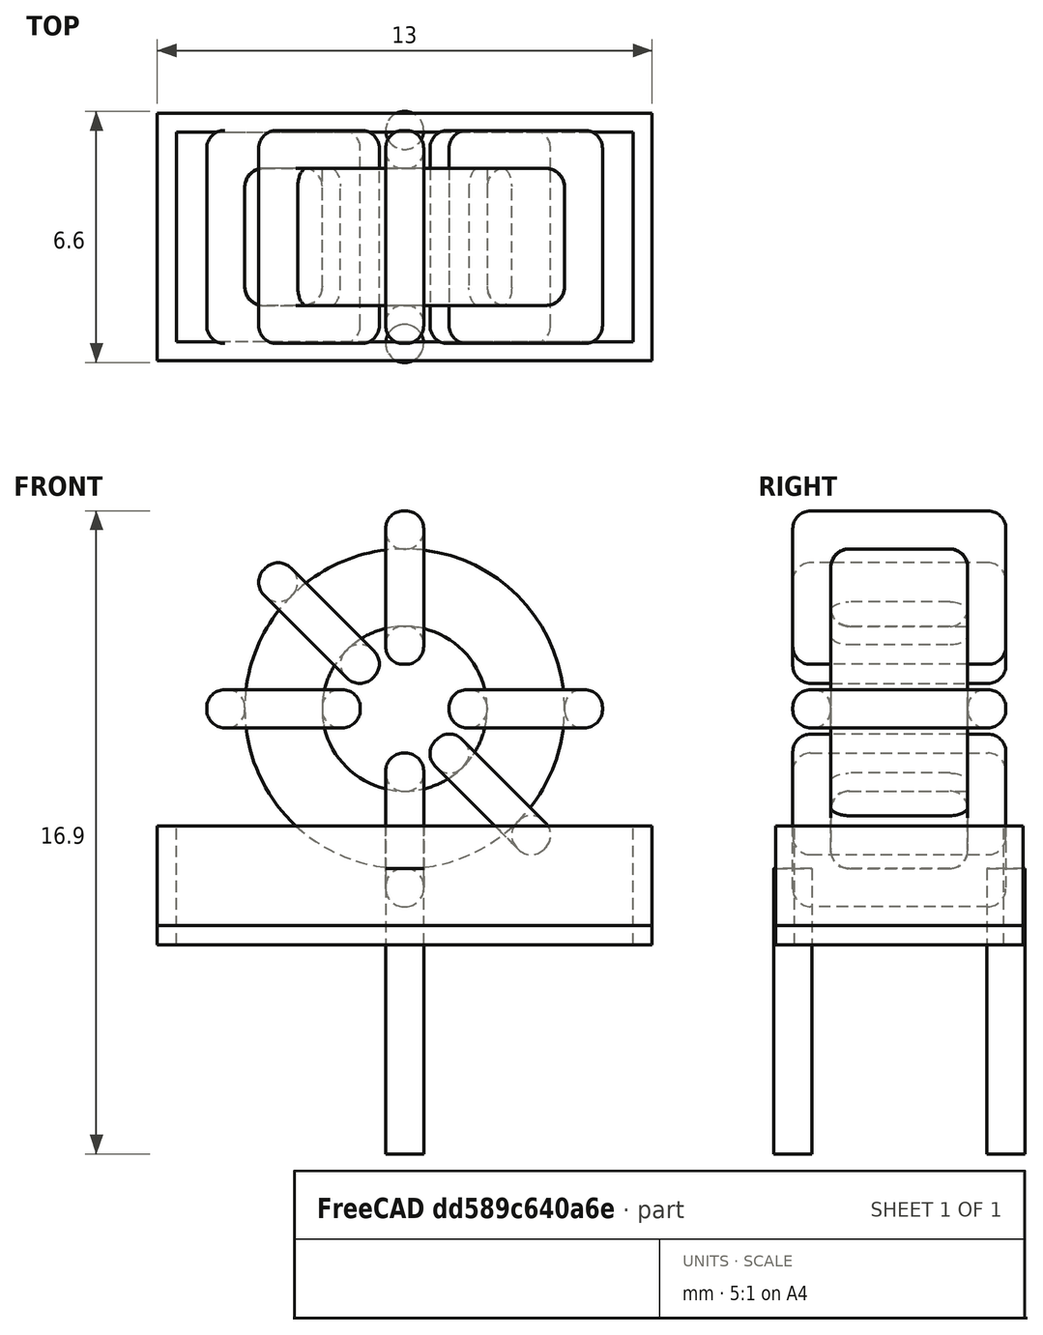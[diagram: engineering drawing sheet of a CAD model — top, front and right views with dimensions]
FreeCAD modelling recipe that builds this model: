
FCSTD DOCUMENT  (FreeCAD 0.16R6703 (Git))
Label: L_Toroid_Vertical_L13.0mm_W6.5mm_P5.60mm
License: All rights reserved
LicenseURL: http://en.wikipedia.org/wiki/All_rights_reserved
objects: Sketcher::SketchObject×8, PartDesign::Pad×8, PartDesign::Fillet×5, Spreadsheet::Sheet×1
note: 29 computed .brp shape members not serialized (recipe doc carries the construction recipe); baked Part::Feature solids carry a one-line shape summary decoded from their .brp

FEATURE [Spreadsheet::Sheet] Spreadsheet  label="dimensions"
  cells = A1=Wx; B1(Wx)=10.4; C1(WW)=4.333333333333333; D1(iWx)=13; A2=Wy; B2(Wy)=5.6; D2(iWy)=6.5; A3=RM; B3(RMx)=5.6; C3(RMy)=0; A4=d_wire; B4(d_wire)=1; A5=H; B5(H)=13; A6=offsetx; B6(offsetx)=6.5
FEATURE [Sketcher::SketchObject] Sketch
  Placement = pos=(0,-2.8,0) rot=(1,0,0;1.5708rad)
  expr: Placement.Base.y = -Spreadsheet.RMx / 2
  expr: Constraints[0] = Spreadsheet.Wx / 2 - Spreadsheet.d_wire
  expr: Constraints[4] = Spreadsheet.WW / 2
  expr: Constraints[2] = Spreadsheet.Wx / 2 + Spreadsheet.d_wire + 0.5
  sketch-geometry (2):
    g0: Circle CenterX=0 CenterY=6.7 CenterZ=0 NormalX=0 NormalY=0 NormalZ=1 Radius=4.2
    g1: Circle CenterX=0 CenterY=6.7 CenterZ=0 NormalX=0 NormalY=0 NormalZ=1 Radius=2.16667
  constraints (5):
    c: Radius(g0) = 4.2
    c: DistanceX(g-1,g0) = 0
    c: DistanceY(g-1,g0) = 6.7
    c: Coincident(g1,g0)
    c: Radius(g1) = 2.16667
FEATURE [PartDesign::Pad] Pad
  Length = 3.6
  Length2 = 100
  Midplane = true
  Placement = pos=(0,-2.8,0) rot=(1,0,0;1.5708rad)
  Sketch = -> Sketch
  Type = 0
  expr: Length = Spreadsheet.Wy - 2 * Spreadsheet.d_wire
FEATURE [Sketcher::SketchObject] Sketch001
  Placement = pos=(0,0,1.5) rot=(0,0,1;0rad)
  expr: Placement.Base.z = 0.5 + Spreadsheet.d_wire
  expr: Constraints[4] = Spreadsheet.RMy
  expr: Constraints[2] = -Spreadsheet.RMx
  expr: Constraints[1] = Spreadsheet.d_wire / 2
  sketch-geometry (2):
    g0: Circle CenterX=0 CenterY=0 CenterZ=0 NormalX=0 NormalY=0 NormalZ=1 Radius=0.5
    g1: Circle CenterX=0 CenterY=-5.6 CenterZ=0 NormalX=0 NormalY=0 NormalZ=1 Radius=0.5
  constraints (5):
    c: Equal(g0,g1)
    c: Radius(g0) = 0.5
    c: DistanceY(g-1,g1) = -5.6
    c: Coincident(g0,g-1)
    c: DistanceX(g-1,g1) = 0
FEATURE [PartDesign::Pad] Pad001
  Length = 1
  Length2 = 6.5
  Placement = pos=(0,0,1.5) rot=(0,0,1;0rad)
  Reversed = true
  Sketch = -> Sketch001
  Type = 4
  expr: Length2 = 5.5 + Spreadsheet.d_wire
  expr: Length = Spreadsheet.d_wire
FEATURE [PartDesign::Fillet] Fillet
  Base = -> Pad [Edge6,Edge3,Edge2]
  Placement = pos=(0,-2.8,0) rot=(1,0,0;1.5708rad)
  Radius = 0.5
FEATURE [Sketcher::SketchObject] Sketch003
  Placement = pos=(0,0,6.7) rot=(1,0,0;3.14159rad)
  expr: Constraints[18] = Spreadsheet.d_wire
  expr: Constraints[16] = Spreadsheet.d_wire
  expr: Constraints[19] = Spreadsheet.d_wire
  expr: Constraints[17] = Spreadsheet.d_wire
  expr: Placement.Base.y = -1 * (Spreadsheet.RMx - Spreadsheet.Wy) / 2
  expr: Constraints[21] = (Spreadsheet.Wx - Spreadsheet.WW) / 2 - Spreadsheet.d_wire
  expr: Constraints[22] = Spreadsheet.Wx / 2 - Spreadsheet.d_wire
  expr: Constraints[43] = Spreadsheet.d_wire
  expr: Constraints[48] = Spreadsheet.Wx - Spreadsheet.d_wire * 2
  expr: Constraints[49] = Spreadsheet.Wy
  expr: Placement.Base.z = Spreadsheet.Wx / 2 + Spreadsheet.d_wire + 0.5
  sketch-geometry (16):
    g0: LineSegment StartX=-1.16667 StartY=0 StartZ=0 EndX=-5.2 EndY=0 EndZ=0
    g1: LineSegment StartX=-5.2 StartY=0 StartZ=0 EndX=-5.2 EndY=5.6 EndZ=0
    g2: LineSegment StartX=-5.2 StartY=5.6 StartZ=0 EndX=-1.16667 EndY=5.6 EndZ=0
    g3: LineSegment StartX=-1.16667 StartY=5.6 StartZ=0 EndX=-1.16667 EndY=0 EndZ=0
    g4: LineSegment StartX=-4.2 StartY=4.6 StartZ=0 EndX=-2.16667 EndY=4.6 EndZ=0
    g5: LineSegment StartX=-2.16667 StartY=4.6 StartZ=0 EndX=-2.16667 EndY=1 EndZ=0
    g6: LineSegment StartX=-2.16667 StartY=1 StartZ=0 EndX=-4.2 EndY=1 EndZ=0
    g7: LineSegment StartX=-4.2 StartY=1 StartZ=0 EndX=-4.2 EndY=4.6 EndZ=0
    g8: LineSegment StartX=1.16667 StartY=5.6 StartZ=0 EndX=5.2 EndY=5.6 EndZ=0
    g9: LineSegment StartX=5.2 StartY=5.6 StartZ=0 EndX=5.2 EndY=0 EndZ=0
    g10: LineSegment StartX=5.2 StartY=0 StartZ=0 EndX=1.16667 EndY=0 EndZ=0
    g11: LineSegment StartX=1.16667 StartY=0 StartZ=0 EndX=1.16667 EndY=5.6 EndZ=0
    g12: LineSegment StartX=2.16667 StartY=4.6 StartZ=0 EndX=4.2 EndY=4.6 EndZ=0
    g13: LineSegment StartX=4.2 StartY=4.6 StartZ=0 EndX=4.2 EndY=1 EndZ=0
    g14: LineSegment StartX=4.2 StartY=1 StartZ=0 EndX=2.16667 EndY=1 EndZ=0
    g15: LineSegment StartX=2.16667 StartY=1 StartZ=0 EndX=2.16667 EndY=4.6 EndZ=0
  constraints (50):
    c: Horizontal(g0)
    c: Coincident(g1,g0)
    c: Vertical(g1)
    c: Coincident(g2,g1)
    c: Horizontal(g2)
    c: Coincident(g3,g2)
    c: Coincident(g3,g0)
    c: Vertical(g3)
    c: Coincident(g4,g5)
    c: Coincident(g5,g6)
    c: Coincident(g6,g7)
    c: Coincident(g7,g4)
    c: Horizontal(g4)
    c: Horizontal(g6)
    c: Vertical(g5)
    c: Vertical(g7)
    c: DistanceX(g1,g4) = 1
    c: DistanceY(g4,g1) = 1
    c: DistanceX(g5,g0) = 1
    c: DistanceY(g0,g5) = 1
    c: DistanceY(g-1,g0) = 0
    c: DistanceX(g6,g6) = 2.03333
    c: DistanceX(g6,g-1) = 4.2
    c: Coincident(g8,g9)
    c: Coincident(g9,g10)
    c: Coincident(g10,g11)
    c: Coincident(g11,g8)
    c: Horizontal(g8)
    c: Horizontal(g10)
    c: Vertical(g9)
    c: Vertical(g11)
    c: Coincident(g12,g13)
    c: Coincident(g13,g14)
    c: Coincident(g14,g15)
    c: Coincident(g15,g12)
    c: Horizontal(g12)
    c: Horizontal(g14)
    c: Vertical(g13)
    c: Vertical(g15)
    c: DistanceY(g8,g2) = 0
    c: DistanceY(g10,g0) = 0
    c: DistanceY(g14,g5) = 0
    c: DistanceY(g12,g4) = 0
    c: DistanceX(g8,g12) = 1
    c: Equal(g8,g2)
    c: Equal(g12,g4)
    c: Equal(g9,g1)
    c: Equal(g13,g7)
    c: DistanceX(g4,g12) = 8.4
    c: DistanceY(g0,g1) = 5.6
FEATURE [PartDesign::Pad] Pad002
  Length = 1
  Length2 = 100
  Midplane = true
  Placement = pos=(0,0,6.7) rot=(1,0,0;3.14159rad)
  Sketch = -> Sketch003
  Type = 0
  expr: Length = Spreadsheet.d_wire
FEATURE [PartDesign::Fillet] Fillet001
  Base = -> Pad002 [Edge38,Edge41,Edge42,Edge43,Edge29,Edge32,Edge33,Edge34,Edge25,Edge35,Edge36,Edge13,Edge14,Edge15,Edge16,Edge17,Edge18,Edge19,Edge1,Edge2,Edge3,Edge4,Edge5,Edge6,Edge7,Edge37,Edge39,Edge40,Edge20,Edge23,Edge24,Edge21,Edge22,Edge8,Edge9,Edge10,Edge11,Edge12,Edge26,Edge27,+8 more]
  Placement = pos=(0,0,6.7) rot=(1,0,0;3.14159rad)
  Radius = 0.47
  expr: Radius = Spreadsheet.d_wire * 0.47
FEATURE [Sketcher::SketchObject] Sketch004
  Placement = pos=(0,0,6.7) rot=(0.92388,0,0.382683;3.14159rad)
  expr: Constraints[18] = Spreadsheet.d_wire
  expr: Constraints[16] = Spreadsheet.d_wire
  expr: Constraints[19] = Spreadsheet.d_wire
  expr: Constraints[17] = Spreadsheet.d_wire
  expr: Placement.Base.y = -1 * (Spreadsheet.RMx - Spreadsheet.Wy) / 2
  expr: Constraints[21] = (Spreadsheet.Wx - Spreadsheet.WW) / 2 - Spreadsheet.d_wire
  expr: Constraints[22] = Spreadsheet.Wx / 2 - Spreadsheet.d_wire
  expr: Constraints[43] = Spreadsheet.d_wire
  expr: Constraints[48] = Spreadsheet.Wx - 2 * Spreadsheet.d_wire
  expr: Constraints[49] = Spreadsheet.Wy
  expr: Placement.Base.z = Spreadsheet.Wx / 2 + Spreadsheet.d_wire + 0.5
  sketch-geometry (16):
    g0: LineSegment StartX=-1.16667 StartY=0 StartZ=0 EndX=-5.2 EndY=0 EndZ=0
    g1: LineSegment StartX=-5.2 StartY=0 StartZ=0 EndX=-5.2 EndY=5.6 EndZ=0
    g2: LineSegment StartX=-5.2 StartY=5.6 StartZ=0 EndX=-1.16667 EndY=5.6 EndZ=0
    g3: LineSegment StartX=-1.16667 StartY=5.6 StartZ=0 EndX=-1.16667 EndY=0 EndZ=0
    g4: LineSegment StartX=-4.2 StartY=4.6 StartZ=0 EndX=-2.16667 EndY=4.6 EndZ=0
    g5: LineSegment StartX=-2.16667 StartY=4.6 StartZ=0 EndX=-2.16667 EndY=1 EndZ=0
    g6: LineSegment StartX=-2.16667 StartY=1 StartZ=0 EndX=-4.2 EndY=1 EndZ=0
    g7: LineSegment StartX=-4.2 StartY=1 StartZ=0 EndX=-4.2 EndY=4.6 EndZ=0
    g8: LineSegment StartX=1.16667 StartY=5.6 StartZ=0 EndX=5.2 EndY=5.6 EndZ=0
    g9: LineSegment StartX=5.2 StartY=5.6 StartZ=0 EndX=5.2 EndY=0 EndZ=0
    g10: LineSegment StartX=5.2 StartY=0 StartZ=0 EndX=1.16667 EndY=0 EndZ=0
    g11: LineSegment StartX=1.16667 StartY=0 StartZ=0 EndX=1.16667 EndY=5.6 EndZ=0
    g12: LineSegment StartX=2.16667 StartY=4.6 StartZ=0 EndX=4.2 EndY=4.6 EndZ=0
    g13: LineSegment StartX=4.2 StartY=4.6 StartZ=0 EndX=4.2 EndY=1 EndZ=0
    g14: LineSegment StartX=4.2 StartY=1 StartZ=0 EndX=2.16667 EndY=1 EndZ=0
    g15: LineSegment StartX=2.16667 StartY=1 StartZ=0 EndX=2.16667 EndY=4.6 EndZ=0
  constraints (50):
    c: Horizontal(g0)
    c: Coincident(g1,g0)
    c: Vertical(g1)
    c: Coincident(g2,g1)
    c: Horizontal(g2)
    c: Coincident(g3,g2)
    c: Coincident(g3,g0)
    c: Vertical(g3)
    c: Coincident(g4,g5)
    c: Coincident(g5,g6)
    c: Coincident(g6,g7)
    c: Coincident(g7,g4)
    c: Horizontal(g4)
    c: Horizontal(g6)
    c: Vertical(g5)
    c: Vertical(g7)
    c: DistanceX(g1,g4) = 1
    c: DistanceY(g4,g1) = 1
    c: DistanceX(g5,g0) = 1
    c: DistanceY(g0,g5) = 1
    c: DistanceY(g-1,g0) = 0
    c: DistanceX(g6,g6) = 2.03333
    c: DistanceX(g6,g-1) = 4.2
    c: Coincident(g8,g9)
    c: Coincident(g9,g10)
    c: Coincident(g10,g11)
    c: Coincident(g11,g8)
    c: Horizontal(g8)
    c: Horizontal(g10)
    c: Vertical(g9)
    c: Vertical(g11)
    c: Coincident(g12,g13)
    c: Coincident(g13,g14)
    c: Coincident(g14,g15)
    c: Coincident(g15,g12)
    c: Horizontal(g12)
    c: Horizontal(g14)
    c: Vertical(g13)
    c: Vertical(g15)
    c: DistanceY(g8,g2) = 0
    c: DistanceY(g10,g0) = 0
    c: DistanceY(g14,g5) = 0
    c: DistanceY(g12,g4) = 0
    c: DistanceX(g8,g12) = 1
    c: Equal(g8,g2)
    c: Equal(g12,g4)
    c: Equal(g9,g1)
    c: Equal(g13,g7)
    c: DistanceX(g4,g12) = 8.4
    c: DistanceY(g0,g1) = 5.6
FEATURE [PartDesign::Pad] Pad003
  Length = 1
  Length2 = 100
  Midplane = true
  Placement = pos=(0,0,6.7) rot=(0.92388,0,0.382683;3.14159rad)
  Sketch = -> Sketch004
  Type = 0
  expr: Length = Spreadsheet.d_wire
FEATURE [PartDesign::Fillet] Fillet002
  Base = -> Pad003 [Edge38,Edge41,Edge42,Edge43,Edge29,Edge32,Edge33,Edge34,Edge25,Edge35,Edge36,Edge13,Edge14,Edge15,Edge16,Edge17,Edge18,Edge19,Edge1,Edge2,Edge3,Edge4,Edge5,Edge6,Edge7,Edge37,Edge39,Edge40,Edge20,Edge23,Edge24,Edge21,Edge22,Edge8,Edge9,Edge10,Edge11,Edge12,Edge26,Edge27,+8 more]
  Placement = pos=(0,0,6.7) rot=(0.92388,0,0.382683;3.14159rad)
  Radius = 0.47
  expr: Radius = Spreadsheet.d_wire * 0.47
FEATURE [Sketcher::SketchObject] Sketch005
  Placement = pos=(0,0,6.7) rot=(0.92388,0,-0.382683;3.14159rad)
  expr: Constraints[18] = Spreadsheet.d_wire
  expr: Constraints[16] = Spreadsheet.d_wire
  expr: Constraints[19] = Spreadsheet.d_wire
  expr: Constraints[17] = Spreadsheet.d_wire
  expr: Placement.Base.y = -1 * (Spreadsheet.RMx - Spreadsheet.Wy) / 2
  expr: Constraints[21] = (Spreadsheet.Wx - Spreadsheet.WW) / 2 - Spreadsheet.d_wire
  expr: Constraints[22] = Spreadsheet.Wx / 2 - Spreadsheet.d_wire
  expr: Constraints[43] = Spreadsheet.d_wire
  expr: Constraints[48] = Spreadsheet.Wx - 2 * Spreadsheet.d_wire
  expr: Constraints[49] = Spreadsheet.Wy
  expr: Placement.Base.z = Spreadsheet.Wx / 2 + Spreadsheet.d_wire + 0.5
  sketch-geometry (16):
    g0: LineSegment StartX=-1.16667 StartY=0 StartZ=0 EndX=-5.2 EndY=0 EndZ=0
    g1: LineSegment StartX=-5.2 StartY=0 StartZ=0 EndX=-5.2 EndY=5.6 EndZ=0
    g2: LineSegment StartX=-5.2 StartY=5.6 StartZ=0 EndX=-1.16667 EndY=5.6 EndZ=0
    g3: LineSegment StartX=-1.16667 StartY=5.6 StartZ=0 EndX=-1.16667 EndY=0 EndZ=0
    g4: LineSegment StartX=-4.2 StartY=4.6 StartZ=0 EndX=-2.16667 EndY=4.6 EndZ=0
    g5: LineSegment StartX=-2.16667 StartY=4.6 StartZ=0 EndX=-2.16667 EndY=1 EndZ=0
    g6: LineSegment StartX=-2.16667 StartY=1 StartZ=0 EndX=-4.2 EndY=1 EndZ=0
    g7: LineSegment StartX=-4.2 StartY=1 StartZ=0 EndX=-4.2 EndY=4.6 EndZ=0
    g8: LineSegment StartX=1.16667 StartY=5.6 StartZ=0 EndX=5.2 EndY=5.6 EndZ=0
    g9: LineSegment StartX=5.2 StartY=5.6 StartZ=0 EndX=5.2 EndY=0 EndZ=0
    g10: LineSegment StartX=5.2 StartY=0 StartZ=0 EndX=1.16667 EndY=0 EndZ=0
    g11: LineSegment StartX=1.16667 StartY=0 StartZ=0 EndX=1.16667 EndY=5.6 EndZ=0
    g12: LineSegment StartX=2.16667 StartY=4.6 StartZ=0 EndX=4.2 EndY=4.6 EndZ=0
    g13: LineSegment StartX=4.2 StartY=4.6 StartZ=0 EndX=4.2 EndY=1 EndZ=0
    g14: LineSegment StartX=4.2 StartY=1 StartZ=0 EndX=2.16667 EndY=1 EndZ=0
    g15: LineSegment StartX=2.16667 StartY=1 StartZ=0 EndX=2.16667 EndY=4.6 EndZ=0
  constraints (50):
    c: Horizontal(g0)
    c: Coincident(g1,g0)
    c: Vertical(g1)
    c: Coincident(g2,g1)
    c: Horizontal(g2)
    c: Coincident(g3,g2)
    c: Coincident(g3,g0)
    c: Vertical(g3)
    c: Coincident(g4,g5)
    c: Coincident(g5,g6)
    c: Coincident(g6,g7)
    c: Coincident(g7,g4)
    c: Horizontal(g4)
    c: Horizontal(g6)
    c: Vertical(g5)
    c: Vertical(g7)
    c: DistanceX(g1,g4) = 1
    c: DistanceY(g4,g1) = 1
    c: DistanceX(g5,g0) = 1
    c: DistanceY(g0,g5) = 1
    c: DistanceY(g-1,g0) = 0
    c: DistanceX(g6,g6) = 2.03333
    c: DistanceX(g6,g-1) = 4.2
    c: Coincident(g8,g9)
    c: Coincident(g9,g10)
    c: Coincident(g10,g11)
    c: Coincident(g11,g8)
    c: Horizontal(g8)
    c: Horizontal(g10)
    c: Vertical(g9)
    c: Vertical(g11)
    c: Coincident(g12,g13)
    c: Coincident(g13,g14)
    c: Coincident(g14,g15)
    c: Coincident(g15,g12)
    c: Horizontal(g12)
    c: Horizontal(g14)
    c: Vertical(g13)
    c: Vertical(g15)
    c: DistanceY(g8,g2) = 0
    c: DistanceY(g10,g0) = 0
    c: DistanceY(g14,g5) = 0
    c: DistanceY(g12,g4) = 0
    c: DistanceX(g8,g12) = 1
    c: Equal(g8,g2)
    c: Equal(g12,g4)
    c: Equal(g9,g1)
    c: Equal(g13,g7)
    c: DistanceX(g4,g12) = 8.4
    c: DistanceY(g0,g1) = 5.6
FEATURE [PartDesign::Pad] Pad004
  Length = 1
  Length2 = 100
  Midplane = true
  Placement = pos=(0,0,6.7) rot=(0.92388,0,-0.382683;3.14159rad)
  Sketch = -> Sketch005
  Type = 0
  expr: Length = Spreadsheet.d_wire
FEATURE [PartDesign::Fillet] Fillet003
  Base = -> Pad004 [Edge38,Edge41,Edge42,Edge43,Edge29,Edge32,Edge33,Edge34,Edge25,Edge35,Edge36,Edge13,Edge14,Edge15,Edge16,Edge17,Edge18,Edge19,Edge1,Edge2,Edge3,Edge4,Edge5,Edge6,Edge7,Edge37,Edge39,Edge40,Edge20,Edge23,Edge24,Edge21,Edge22,Edge8,Edge9,Edge10,Edge11,Edge12,Edge26,Edge27,+8 more]
  Placement = pos=(0,0,6.7) rot=(0.92388,0,-0.382683;3.14159rad)
  Radius = 0.47
  expr: Radius = Spreadsheet.d_wire * 0.47
FEATURE [Sketcher::SketchObject] Sketch006
  Placement = pos=(0,0,6.7) rot=(0.707107,0,0.707107;3.14159rad)
  expr: Constraints[18] = Spreadsheet.d_wire
  expr: Constraints[16] = Spreadsheet.d_wire
  expr: Constraints[19] = Spreadsheet.d_wire
  expr: Constraints[17] = Spreadsheet.d_wire
  expr: Placement.Base.y = -1 * (Spreadsheet.RMx - Spreadsheet.Wy) / 2
  expr: Constraints[21] = (Spreadsheet.Wx - Spreadsheet.WW) / 2 - Spreadsheet.d_wire
  expr: Constraints[22] = Spreadsheet.Wx / 2 - Spreadsheet.d_wire
  expr: Constraints[43] = Spreadsheet.d_wire
  expr: Constraints[48] = Spreadsheet.Wx - Spreadsheet.d_wire * 2
  expr: Constraints[49] = Spreadsheet.Wy
  expr: Placement.Base.z = Spreadsheet.Wx / 2 + Spreadsheet.d_wire + 0.5
  sketch-geometry (16):
    g0: LineSegment StartX=-1.16667 StartY=0 StartZ=0 EndX=-5.2 EndY=0 EndZ=0
    g1: LineSegment StartX=-5.2 StartY=0 StartZ=0 EndX=-5.2 EndY=5.6 EndZ=0
    g2: LineSegment StartX=-5.2 StartY=5.6 StartZ=0 EndX=-1.16667 EndY=5.6 EndZ=0
    g3: LineSegment StartX=-1.16667 StartY=5.6 StartZ=0 EndX=-1.16667 EndY=0 EndZ=0
    g4: LineSegment StartX=-4.2 StartY=4.6 StartZ=0 EndX=-2.16667 EndY=4.6 EndZ=0
    g5: LineSegment StartX=-2.16667 StartY=4.6 StartZ=0 EndX=-2.16667 EndY=1 EndZ=0
    g6: LineSegment StartX=-2.16667 StartY=1 StartZ=0 EndX=-4.2 EndY=1 EndZ=0
    g7: LineSegment StartX=-4.2 StartY=1 StartZ=0 EndX=-4.2 EndY=4.6 EndZ=0
    g8: LineSegment StartX=1.16667 StartY=5.6 StartZ=0 EndX=5.2 EndY=5.6 EndZ=0
    g9: LineSegment StartX=5.2 StartY=5.6 StartZ=0 EndX=5.2 EndY=0 EndZ=0
    g10: LineSegment StartX=5.2 StartY=0 StartZ=0 EndX=1.16667 EndY=0 EndZ=0
    g11: LineSegment StartX=1.16667 StartY=0 StartZ=0 EndX=1.16667 EndY=5.6 EndZ=0
    g12: LineSegment StartX=2.16667 StartY=4.6 StartZ=0 EndX=4.2 EndY=4.6 EndZ=0
    g13: LineSegment StartX=4.2 StartY=4.6 StartZ=0 EndX=4.2 EndY=1 EndZ=0
    g14: LineSegment StartX=4.2 StartY=1 StartZ=0 EndX=2.16667 EndY=1 EndZ=0
    g15: LineSegment StartX=2.16667 StartY=1 StartZ=0 EndX=2.16667 EndY=4.6 EndZ=0
  constraints (50):
    c: Horizontal(g0)
    c: Coincident(g1,g0)
    c: Vertical(g1)
    c: Coincident(g2,g1)
    c: Horizontal(g2)
    c: Coincident(g3,g2)
    c: Coincident(g3,g0)
    c: Vertical(g3)
    c: Coincident(g4,g5)
    c: Coincident(g5,g6)
    c: Coincident(g6,g7)
    c: Coincident(g7,g4)
    c: Horizontal(g4)
    c: Horizontal(g6)
    c: Vertical(g5)
    c: Vertical(g7)
    c: DistanceX(g1,g4) = 1
    c: DistanceY(g4,g1) = 1
    c: DistanceX(g5,g0) = 1
    c: DistanceY(g0,g5) = 1
    c: DistanceY(g-1,g0) = 0
    c: DistanceX(g6,g6) = 2.03333
    c: DistanceX(g6,g-1) = 4.2
    c: Coincident(g8,g9)
    c: Coincident(g9,g10)
    c: Coincident(g10,g11)
    c: Coincident(g11,g8)
    c: Horizontal(g8)
    c: Horizontal(g10)
    c: Vertical(g9)
    c: Vertical(g11)
    c: Coincident(g12,g13)
    c: Coincident(g13,g14)
    c: Coincident(g14,g15)
    c: Coincident(g15,g12)
    c: Horizontal(g12)
    c: Horizontal(g14)
    c: Vertical(g13)
    c: Vertical(g15)
    c: DistanceY(g8,g2) = 0
    c: DistanceY(g10,g0) = 0
    c: DistanceY(g14,g5) = 0
    c: DistanceY(g12,g4) = 0
    c: DistanceX(g8,g12) = 1
    c: Equal(g8,g2)
    c: Equal(g12,g4)
    c: Equal(g9,g1)
    c: Equal(g13,g7)
    c: DistanceX(g4,g12) = 8.4
    c: DistanceY(g0,g1) = 5.6
FEATURE [PartDesign::Pad] Pad005
  Length = 1
  Length2 = 100
  Midplane = true
  Placement = pos=(0,0,6.7) rot=(0.707107,0,0.707107;3.14159rad)
  Sketch = -> Sketch006
  Type = 0
  expr: Length = Spreadsheet.d_wire
FEATURE [PartDesign::Fillet] Fillet004
  Base = -> Pad005 [Edge38,Edge41,Edge42,Edge43,Edge29,Edge32,Edge33,Edge34,Edge25,Edge35,Edge36,Edge13,Edge14,Edge15,Edge16,Edge17,Edge18,Edge19,Edge1,Edge2,Edge3,Edge4,Edge5,Edge6,Edge7,Edge37,Edge39,Edge40,Edge20,Edge23,Edge24,Edge21,Edge22,Edge8,Edge9,Edge10,Edge11,Edge12,Edge26,Edge27,+8 more]
  Placement = pos=(0,0,6.7) rot=(0.707107,0,0.707107;3.14159rad)
  Radius = 0.47
  expr: Radius = Spreadsheet.d_wire * 0.47
FEATURE [Sketcher::SketchObject] Sketch007
  Placement = pos=(0,0,0.5) rot=(0,0,1;0rad)
  expr: Placement.Base.z = 0.5
  expr: Constraints[11] = Spreadsheet.iWx / 2
  expr: Constraints[10] = (Spreadsheet.iWy - Spreadsheet.RMx) / 2
  expr: Constraints[9] = Spreadsheet.iWy
  expr: Constraints[8] = Spreadsheet.iWx
  sketch-geometry (4):
    g0: LineSegment StartX=-6.5 StartY=0.45 StartZ=0 EndX=6.5 EndY=0.45 EndZ=0
    g1: LineSegment StartX=6.5 StartY=0.45 StartZ=0 EndX=6.5 EndY=-6.05 EndZ=0
    g2: LineSegment StartX=6.5 StartY=-6.05 StartZ=0 EndX=-6.5 EndY=-6.05 EndZ=0
    g3: LineSegment StartX=-6.5 StartY=-6.05 StartZ=0 EndX=-6.5 EndY=0.45 EndZ=0
  constraints (12):
    c: Coincident(g0,g1)
    c: Coincident(g1,g2)
    c: Coincident(g2,g3)
    c: Coincident(g3,g0)
    c: Horizontal(g0)
    c: Horizontal(g2)
    c: Vertical(g1)
    c: Vertical(g3)
    c: DistanceX(g0,g0) = 13
    c: DistanceY(g3,g3) = 6.5
    c: DistanceY(g-1,g0) = 0.45
    c: DistanceX(g0,g-1) = 6.5
FEATURE [PartDesign::Pad] Pad006
  Length = 0.5
  Length2 = 100
  Placement = pos=(0,0,0.5) rot=(0,0,1;0rad)
  Sketch = -> Sketch007
  Type = 0
FEATURE [Sketcher::SketchObject] Sketch008
  Placement = pos=(0,0,0.5) rot=(0,0,1;0rad)
  expr: Constraints[8] = Spreadsheet.iWx
  expr: Constraints[9] = Spreadsheet.iWy
  expr: Constraints[10] = (Spreadsheet.iWy - Spreadsheet.RMx) / 2
  expr: Placement.Base.z = 0.5
  expr: Constraints[21] = 0.5
  expr: Constraints[11] = Spreadsheet.iWx / 2
  sketch-geometry (8):
    g0: LineSegment StartX=-6.5 StartY=0.45 StartZ=0 EndX=6.5 EndY=0.45 EndZ=0
    g1: LineSegment StartX=6.5 StartY=0.45 StartZ=0 EndX=6.5 EndY=-6.05 EndZ=0
    g2: LineSegment StartX=6.5 StartY=-6.05 StartZ=0 EndX=-6.5 EndY=-6.05 EndZ=0
    g3: LineSegment StartX=-6.5 StartY=-6.05 StartZ=0 EndX=-6.5 EndY=0.45 EndZ=0
    g4: LineSegment StartX=-6 StartY=-0.05 StartZ=0 EndX=6 EndY=-0.05 EndZ=0
    g5: LineSegment StartX=6 StartY=-0.05 StartZ=0 EndX=6 EndY=-5.55 EndZ=0
    g6: LineSegment StartX=6 StartY=-5.55 StartZ=0 EndX=-6 EndY=-5.55 EndZ=0
    g7: LineSegment StartX=-6 StartY=-5.55 StartZ=0 EndX=-6 EndY=-0.05 EndZ=0
  constraints (24):
    c: Coincident(g0,g1)
    c: Coincident(g1,g2)
    c: Coincident(g2,g3)
    c: Coincident(g3,g0)
    c: Horizontal(g0)
    c: Horizontal(g2)
    c: Vertical(g1)
    c: Vertical(g3)
    c: DistanceX(g0,g0) = 13
    c: DistanceY(g3,g3) = 6.5
    c: DistanceY(g-1,g0) = 0.45
    c: DistanceX(g0,g-1) = 6.5
    c: Coincident(g4,g5)
    c: Coincident(g5,g6)
    c: Coincident(g6,g7)
    c: Coincident(g7,g4)
    c: Horizontal(g4)
    c: Horizontal(g6)
    c: Vertical(g5)
    c: Vertical(g7)
    c: DistanceX(g5,g1) = 0.5
    c: DistanceY(g1,g5) = 0.5
    c: DistanceX(g0,g4) = 0.5
    c: DistanceY(g4,g0) = 0.5
FEATURE [PartDesign::Pad] Pad007
  Length = 3.12
  Length2 = 100
  Placement = pos=(0,0,0.5) rot=(0,0,1;0rad)
  Sketch = -> Sketch008
  Type = 0
  expr: Length = Spreadsheet.Wx * 0.3
